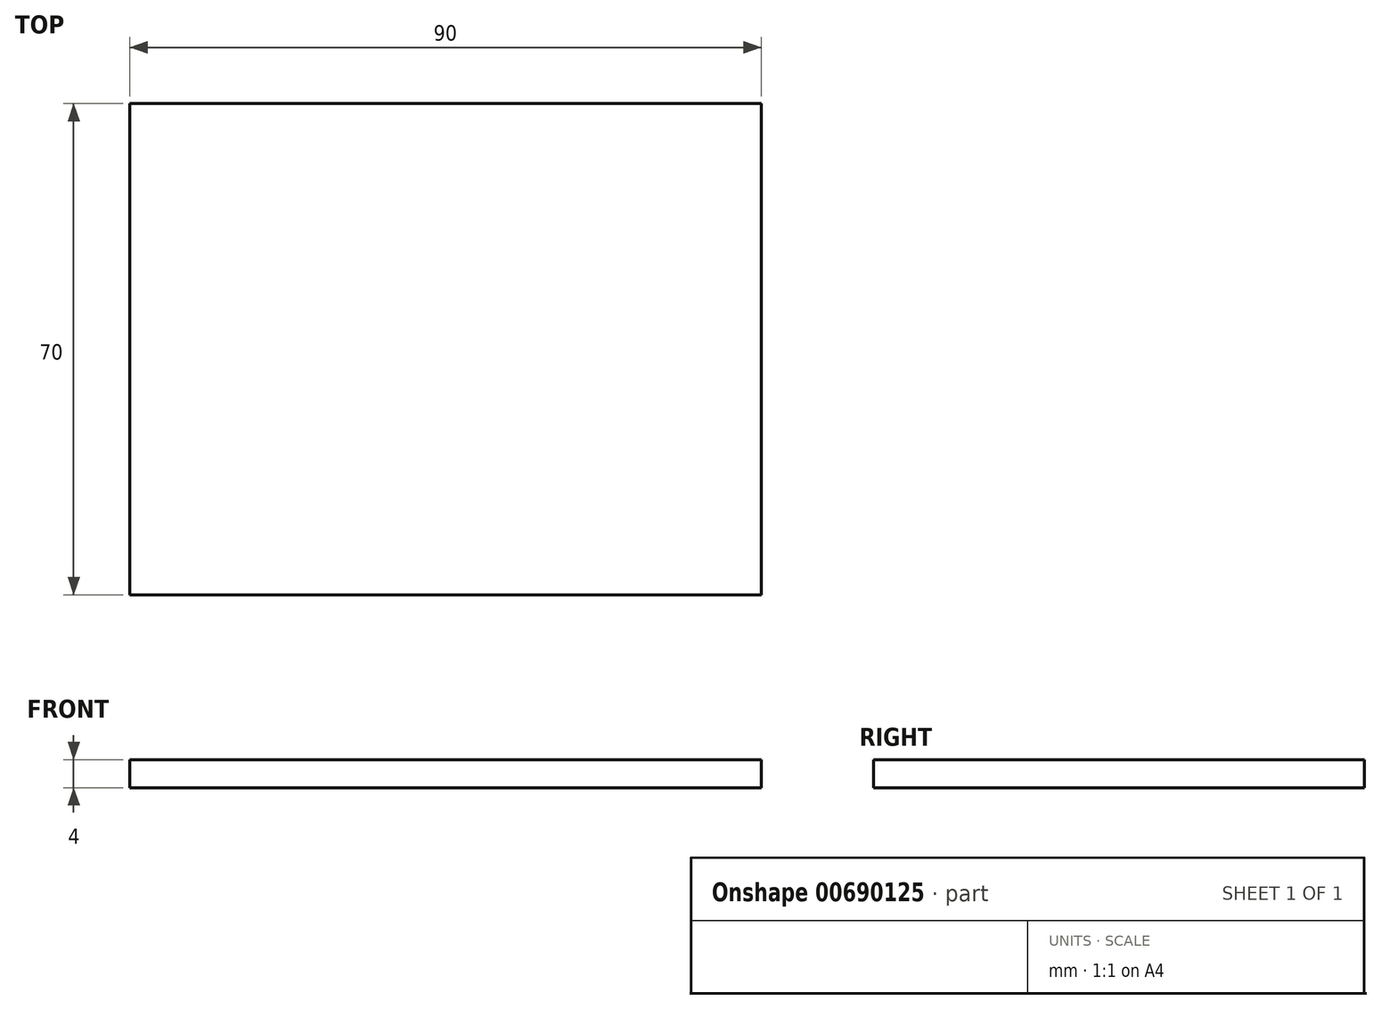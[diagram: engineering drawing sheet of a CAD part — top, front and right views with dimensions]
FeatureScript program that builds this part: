
annotation { "Feature Type Name" : "Feature", "Feature Type Description" : "" }
export const myFeature = defineFeature(function(context is Context, id is Id, definition is map)
    precondition{}
    {
        {
            var Q0;
            Q0=qCreatedBy(makeId("Top.planeOp"),FACE);
            var sketch = newSketch(context, id + "F0", { "sketchPlane" : qUnion([Q0])});
            skLineSegment(sketch, "E0.bottom", {"start": v(-44.3, 32.66) * mm, "end": v(45.7, 32.66) * mm});
            skLineSegment(sketch, "E0.top", {"start": v(-44.3, -37.34) * mm, "end": v(45.7, -37.34) * mm});
            skLineSegment(sketch, "E0.left", {"start": v(-44.3, 32.66) * mm, "end": v(-44.3, -37.34) * mm});
            skLineSegment(sketch, "E0.right", {"start": v(45.7, 32.66) * mm, "end": v(45.7, -37.34) * mm});
            skSolve(sketch);
        }
        {
            var Q0;
            Q0=makeQuery(id+"F0.imprint","IMPRINT",FACE,{"disambiguationData":[TD([[makeQuery(id+"F0.imprint","IMPRINT",EDGE,{"derivedFrom":sQuery(id+"F0.wireOp",EDGE,"E0.bottom")}),-1.0]])]});
            extrude(context, id + "F1", {"entities" : qUnion([Q0]), "depth" : 4 * mm, "offsetDistance" : 25 * mm});
        }
    });
